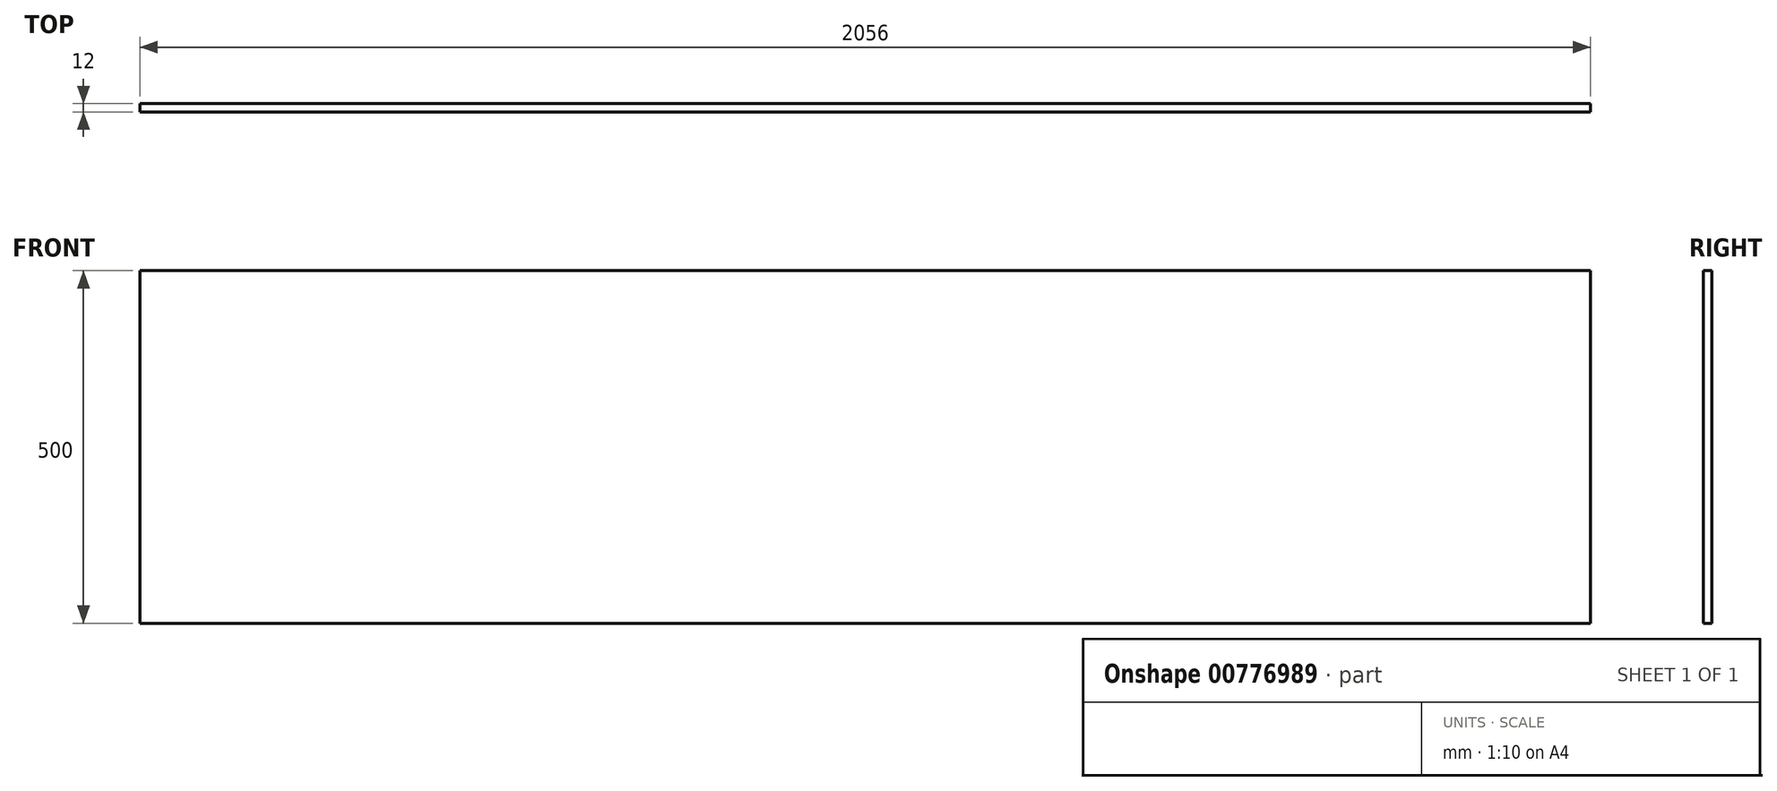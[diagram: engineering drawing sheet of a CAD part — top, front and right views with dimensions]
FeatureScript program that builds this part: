
annotation { "Feature Type Name" : "Feature", "Feature Type Description" : "" }
export const myFeature = defineFeature(function(context is Context, id is Id, definition is map)
    precondition{}
    {
        {
            var Q0;
            Q0=qCreatedBy(makeId("Front.planeOp"),FACE);
            var sketch = newSketch(context, id + "F0", { "sketchPlane" : qUnion([Q0])});
            skLineSegment(sketch, "E0.bottom", {"start": v(-999.97, 192.54) * mm, "end": v(1056.03, 192.54) * mm});
            skLineSegment(sketch, "E0.top", {"start": v(-999.97, -307.46) * mm, "end": v(1056.03, -307.46) * mm});
            skLineSegment(sketch, "E0.left", {"start": v(-999.97, 192.54) * mm, "end": v(-999.97, -307.46) * mm});
            skLineSegment(sketch, "E0.right", {"start": v(1056.03, 192.54) * mm, "end": v(1056.03, -307.46) * mm});
            skSolve(sketch);
        }
        {
            var Q0;
            Q0 = qSketchRegion(id + "F0", true);
            extrude(context, id + "F1", {"entities" : qUnion([Q0]), "depth" : 12 * mm, "offsetDistance" : 25 * mm});
        }
    });
